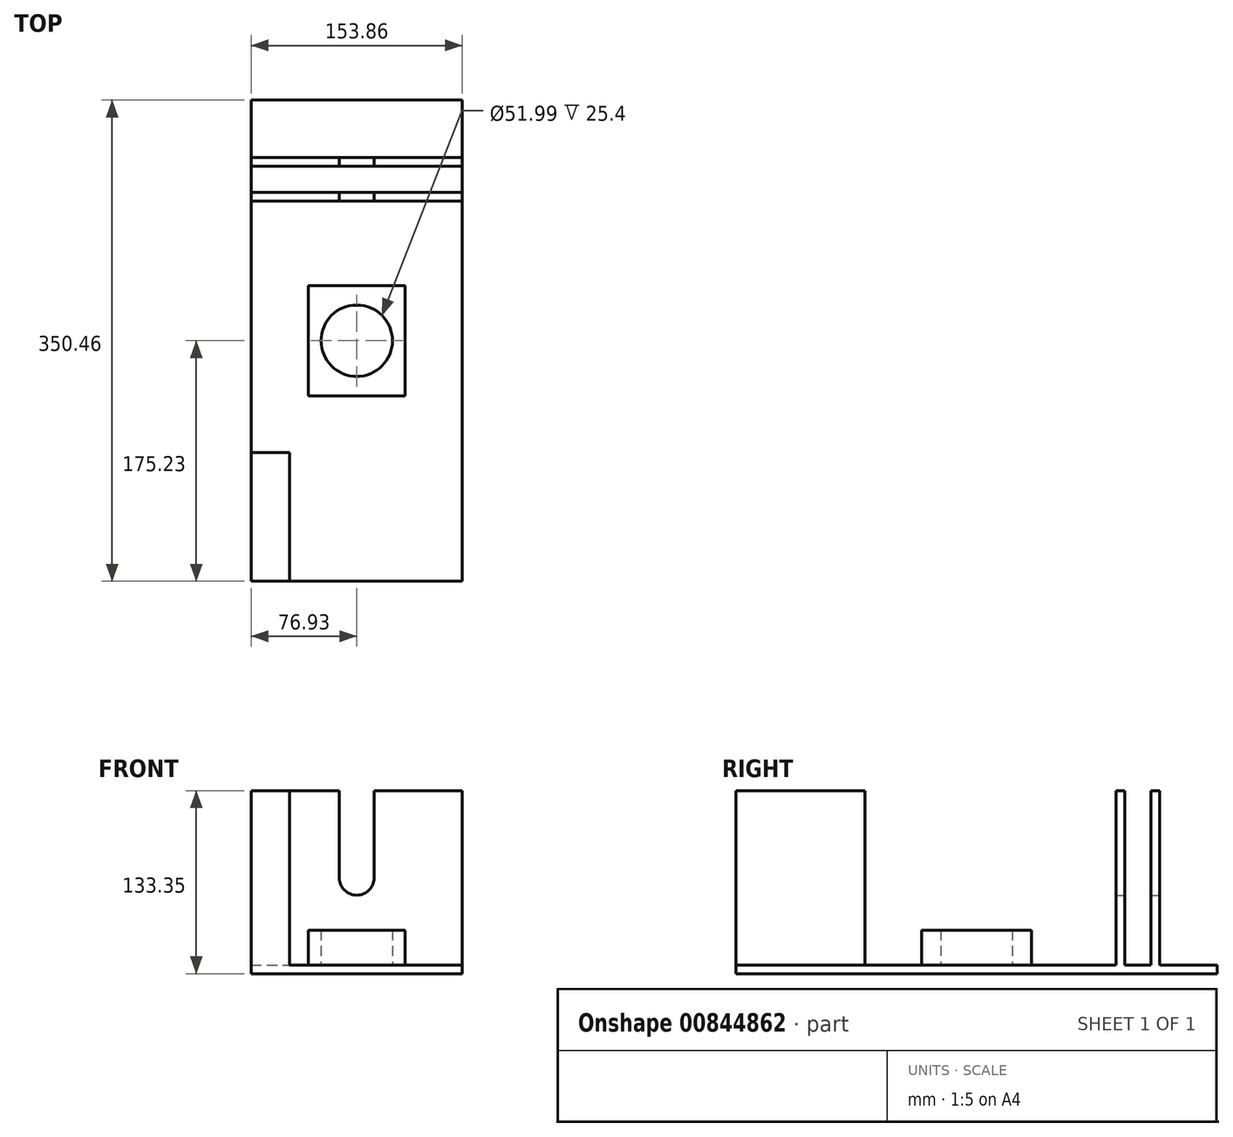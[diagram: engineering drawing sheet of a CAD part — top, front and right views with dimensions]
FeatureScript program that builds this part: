
annotation { "Feature Type Name" : "Feature", "Feature Type Description" : "" }
export const myFeature = defineFeature(function(context is Context, id is Id, definition is map)
    precondition{}
    {
        {
            var Q0;
            Q0=qCreatedBy(makeId("Top.planeOp"),FACE);
            var sketch = newSketch(context, id + "F0", { "sketchPlane" : qUnion([Q0])});
            skLineSegment(sketch, "E0.bottom", {"start": v(76.93, -175.23) * mm, "end": v(-76.93, -175.23) * mm});
            skLineSegment(sketch, "E0.top", {"start": v(76.93, 175.23) * mm, "end": v(-76.93, 175.23) * mm});
            skLineSegment(sketch, "E0.left", {"start": v(76.93, -175.23) * mm, "end": v(76.93, 175.23) * mm});
            skLineSegment(sketch, "E0.right", {"start": v(-76.93, -175.23) * mm, "end": v(-76.93, 175.23) * mm});
            skPoint(sketch, "E0.middle", {"position": v(0, 0) * mm});
            skSolve(sketch);
        }
        {
            var Q0;
            Q0 = qSketchRegion(id + "F0", true);
            extrude(context, id + "F1", {"entities" : qUnion([Q0]), "depth" : 6.35 * mm, "offsetDistance" : 25.4 * mm});
        }
        {
            var Q0;
            Q0=makeQuery(id+"F1.opExtrude","CAP_FACE",FACE,{"disambiguationData":[OSD([sQuery(id+"F0.wireOp",EDGE,"E0.bottom"),sQuery(id+"F0.wireOp",EDGE,"E0.top"),sQuery(id+"F0.wireOp",EDGE,"E0.left"),sQuery(id+"F0.wireOp",EDGE,"E0.right")])],"isStart":false});
            var sketch = newSketch(context, id + "F2", { "sketchPlane" : qUnion([Q0])});
            skLineSegment(sketch, "E1", {"start": v(76.93, 133.35) * mm, "end": v(-76.93, 133.35) * mm});
            skLineSegment(sketch, "E2", {"start": v(76.93, 127) * mm, "end": v(-76.93, 127) * mm});
            skLineSegment(sketch, "E3", {"start": v(-76.93, 127) * mm, "end": v(-76.93, 133.35) * mm});
            skLineSegment(sketch, "E4", {"start": v(76.93, 127) * mm, "end": v(76.93, 133.35) * mm});
            skSolve(sketch);
        }
        {
            var Q0;
            Q0=makeQuery(id+"F2.imprint","IMPRINT",FACE,{"disambiguationData":[TD([[makeQuery(id+"F2.imprint","IMPRINT",EDGE,{"derivedFrom":sQuery(id+"F2.wireOp",EDGE,"E1")}),1.0]])]});
            extrude(context, id + "F3", {"entities" : qUnion([Q0]), "operationType" : NewBodyOperationType.ADD, "depth" : 127 * mm, "offsetDistance" : 25.4 * mm});
        }
        {
            var Q0;
            {var subQ0=sQuery(id+"F0.wireOp",EDGE,"E0.left");var subQ1=sQuery(id+"F0.wireOp",EDGE,"E0.right");var subQ2=sQuery(id+"F0.wireOp",EDGE,"E0.bottom");Q0=makeQuery(id+"F3.boolean.opBoolean","SPLIT",FACE,{"disambiguationData":[TD([makeQuery(id+"F1.opExtrude","SWEPT_FACE",FACE,{"disambiguationData":[OSD([subQ2])]})])],"derivedFrom":makeQuery(id+"F1.opExtrude","CAP_FACE",FACE,{"disambiguationData":[OSD([subQ2,sQuery(id+"F0.wireOp",EDGE,"E0.top"),subQ0,subQ1])],"isStart":false})});}
            var sketch = newSketch(context, id + "F4", { "sketchPlane" : qUnion([Q0])});
            skLineSegment(sketch, "E5", {"start": v(76.93, 107.95) * mm, "end": v(-76.93, 107.95) * mm});
            skLineSegment(sketch, "E6", {"start": v(-76.93, 107.95) * mm, "end": v(-76.93, 101.6) * mm});
            skLineSegment(sketch, "E7", {"start": v(-76.93, 101.6) * mm, "end": v(76.93, 101.6) * mm});
            skLineSegment(sketch, "E8", {"start": v(76.93, 101.6) * mm, "end": v(76.93, 107.95) * mm});
            skSolve(sketch);
        }
        {
            var Q0;
            Q0 = qSketchRegion(id + "F4", true);
            extrude(context, id + "F5", {"entities" : qUnion([Q0]), "operationType" : NewBodyOperationType.ADD, "depth" : 127 * mm, "offsetDistance" : 25.4 * mm});
        }
        {
            var Q0;
            Q0=makeQuery(id+"F3.opExtrude","SWEPT_FACE",FACE,{"disambiguationData":[OSD([sQuery(id+"F2.wireOp",EDGE,"E1")])]});
            var sketch = newSketch(context, id + "F6", { "sketchPlane" : qUnion([Q0])});
            skLineSegment(sketch, "E9", {"start": v(0, 0) * mm, "end": v(0, 133.35) * mm, "construction": true});
            skLineSegment(sketch, "E10", {"start": v(0, 133.35) * mm, "end": v(-12.7, 133.35) * mm});
            skLineSegment(sketch, "E11", {"start": v(0, 133.35) * mm, "end": v(12.7, 133.35) * mm});
            skLineSegment(sketch, "E12", {"start": v(12.7, 133.35) * mm, "end": v(12.7, 69.85) * mm});
            skLineSegment(sketch, "E13", {"start": v(-12.7, 133.35) * mm, "end": v(-12.7, 69.85) * mm});
            skArc(sketch, "E14", {"start": v(-12.7, 69.85) * mm, "mid": v(0, 57.15) * mm, "end": v(12.7, 69.85) * mm});
            skSolve(sketch);
        }
        {
            var Q0;
            Q0=makeQuery(id+"F6.imprint","IMPRINT",FACE,{"disambiguationData":[TD([[makeQuery(id+"F6.imprint","IMPRINT",EDGE,{"derivedFrom":sQuery(id+"F6.wireOp",EDGE,"E10")}),-1.0]])]});
            extrude(context, id + "F7", {"entities" : qUnion([Q0]), "operationType" : NewBodyOperationType.REMOVE, "oppositeDirection" : true, "depth" : 96.77 * mm, "offsetDistance" : 25.4 * mm});
        }
        {
            var Q0;
            {var subQ1=sQuery(id+"F0.wireOp",EDGE,"E0.right");var subQ3=sQuery(id+"F0.wireOp",EDGE,"E0.left");var subQ5=sQuery(id+"F0.wireOp",EDGE,"E0.bottom");var subQ6=makeQuery(id+"F1.opExtrude","SWEPT_FACE",FACE,{"disambiguationData":[OSD([subQ5])]});Q0=makeQuery(id+"F5.boolean.opBoolean","SPLIT",FACE,{"disambiguationData":[TD([subQ6])],"derivedFrom":makeQuery(id+"F3.boolean.opBoolean","SPLIT",FACE,{"disambiguationData":[TD([subQ6])],"derivedFrom":makeQuery(id+"F1.opExtrude","CAP_FACE",FACE,{"disambiguationData":[OSD([subQ5,sQuery(id+"F0.wireOp",EDGE,"E0.top"),subQ3,subQ1])],"isStart":false})})});}
            var sketch = newSketch(context, id + "F8", { "sketchPlane" : qUnion([Q0])});
            skLineSegment(sketch, "E15.bottom", {"start": v(35.22, -40.1) * mm, "end": v(-35.22, -40.1) * mm});
            skLineSegment(sketch, "E15.top", {"start": v(35.22, 40.1) * mm, "end": v(-35.22, 40.1) * mm});
            skLineSegment(sketch, "E15.left", {"start": v(35.22, -40.1) * mm, "end": v(35.22, 40.1) * mm});
            skLineSegment(sketch, "E15.right", {"start": v(-35.22, -40.1) * mm, "end": v(-35.22, 40.1) * mm});
            skPoint(sketch, "E15.middle", {"position": v(0, 0) * mm});
            skCircle(sketch, "E16", {"center": v(0, 0) * mm, "radius": 26 * mm});
            skSolve(sketch);
        }
        {
            var Q0;
            Q0 = qSketchRegion(id + "F8", true);
            extrude(context, id + "F9", {"entities" : qUnion([Q0]), "operationType" : NewBodyOperationType.ADD, "depth" : 25.4 * mm, "offsetDistance" : 25.4 * mm});
        }
        {
            var Q0;
            {var subQ3=sQuery(id+"F0.wireOp",EDGE,"E0.bottom");var subQ4=makeQuery(id+"F1.opExtrude","SWEPT_FACE",FACE,{"disambiguationData":[OSD([subQ3])]});var subQ7=sQuery(id+"F0.wireOp",EDGE,"E0.left");var subQ9=sQuery(id+"F0.wireOp",EDGE,"E0.right");Q0=makeQuery(id+"F9.boolean.opBoolean","SPLIT",FACE,{"disambiguationData":[TD([subQ4])],"derivedFrom":makeQuery(id+"F5.boolean.opBoolean","SPLIT",FACE,{"disambiguationData":[TD([subQ4])],"derivedFrom":makeQuery(id+"F3.boolean.opBoolean","SPLIT",FACE,{"disambiguationData":[TD([subQ4])],"derivedFrom":makeQuery(id+"F1.opExtrude","CAP_FACE",FACE,{"disambiguationData":[OSD([subQ3,sQuery(id+"F0.wireOp",EDGE,"E0.top"),subQ7,subQ9])],"isStart":false})})})});}
            var sketch = newSketch(context, id + "F10", { "sketchPlane" : qUnion([Q0])});
            skLineSegment(sketch, "E17", {"start": v(-76.93, -81.33) * mm, "end": v(-76.93, -175.23) * mm});
            skLineSegment(sketch, "E18", {"start": v(-76.93, -175.23) * mm, "end": v(-48.95, -175.23) * mm});
            skLineSegment(sketch, "E19", {"start": v(-48.95, -175.23) * mm, "end": v(-48.95, -81.33) * mm});
            skLineSegment(sketch, "E20", {"start": v(-48.95, -81.33) * mm, "end": v(-76.93, -81.33) * mm});
            skSolve(sketch);
        }
        {
            var Q0;
            Q0=makeQuery(id+"F10.imprint","IMPRINT",FACE,{"disambiguationData":[TD([[makeQuery(id+"F10.imprint","IMPRINT",EDGE,{"derivedFrom":sQuery(id+"F10.wireOp",EDGE,"E17")}),-1.0]])]});
            extrude(context, id + "F11", {"entities" : qUnion([Q0]), "operationType" : NewBodyOperationType.ADD, "depth" : 127 * mm, "offsetDistance" : 25.4 * mm});
        }
    });
